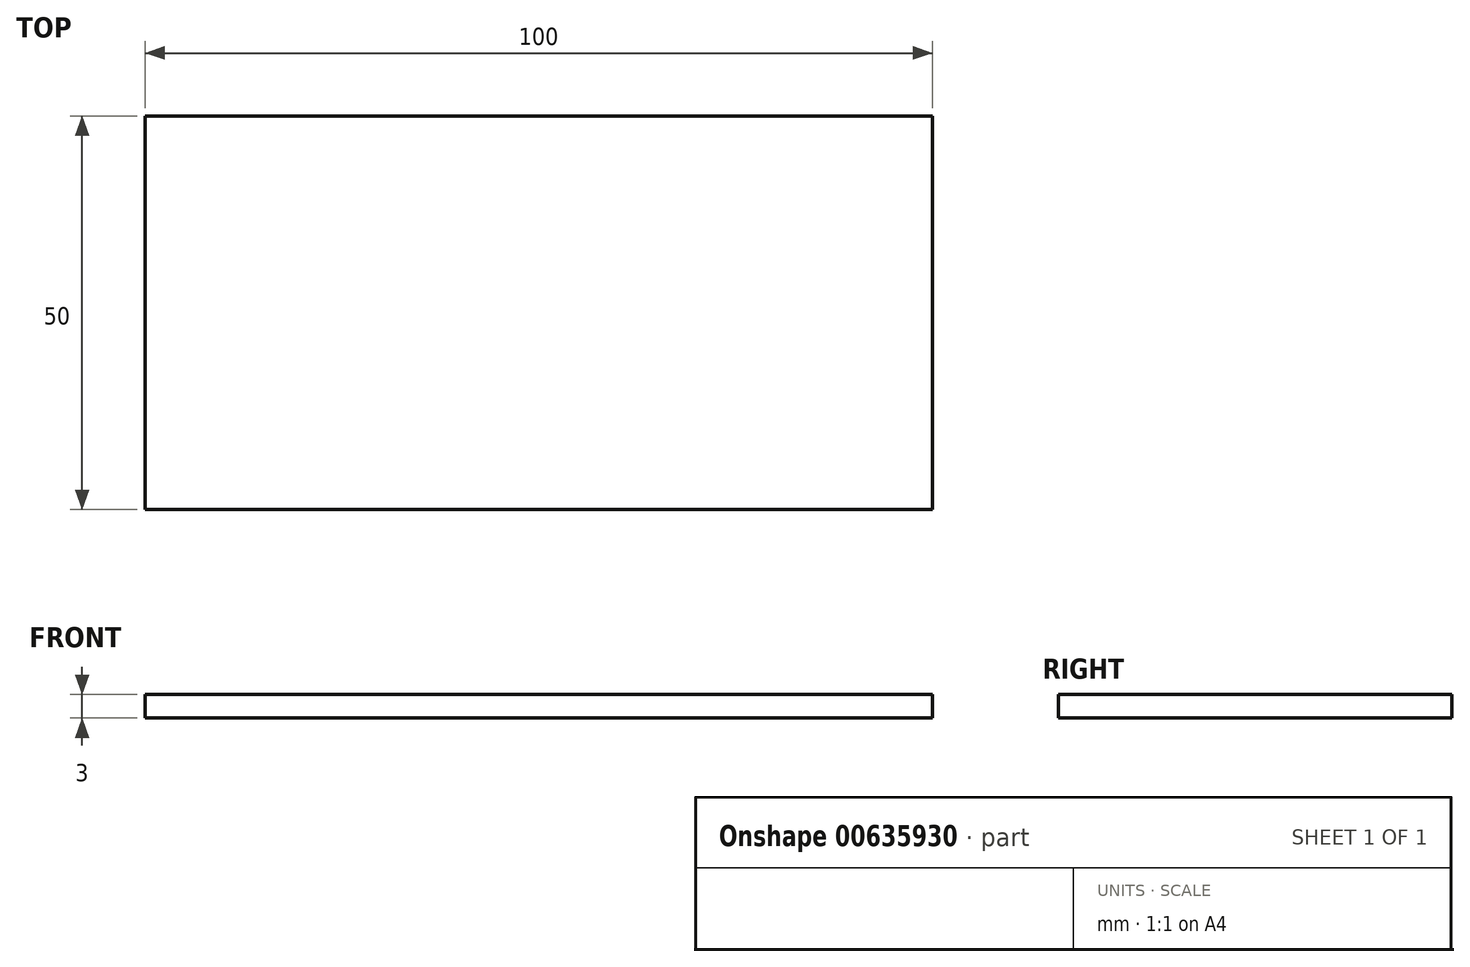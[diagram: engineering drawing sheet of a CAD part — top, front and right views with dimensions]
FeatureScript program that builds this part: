
annotation { "Feature Type Name" : "Feature", "Feature Type Description" : "" }
export const myFeature = defineFeature(function(context is Context, id is Id, definition is map)
    precondition{}
    {
        {
            var Q0;
            Q0=qCreatedBy(makeId("Top.planeOp"),FACE);
            var sketch = newSketch(context, id + "F0", { "sketchPlane" : qUnion([Q0])});
            skLineSegment(sketch, "E0.bottom", {"start": v(-74.1, 38.87) * mm, "end": v(25.9, 38.87) * mm});
            skLineSegment(sketch, "E0.top", {"start": v(-74.1, -11.13) * mm, "end": v(25.9, -11.13) * mm});
            skLineSegment(sketch, "E0.left", {"start": v(-74.1, 38.87) * mm, "end": v(-74.1, -11.13) * mm});
            skLineSegment(sketch, "E0.right", {"start": v(25.9, 38.87) * mm, "end": v(25.9, -11.13) * mm});
            skSolve(sketch);
        }
        {
            var Q0;
            Q0 = qSketchRegion(id + "F0", true);
            extrude(context, id + "F1", {"entities" : qUnion([Q0]), "depth" : 3 * mm, "offsetDistance" : 25 * mm});
        }
    });
